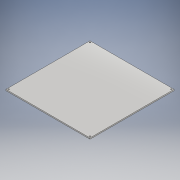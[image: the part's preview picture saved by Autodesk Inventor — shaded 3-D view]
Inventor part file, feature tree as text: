
AUTODESK INVENTOR PART (.ipt)
format: ipt  version: 2017 (Build 210142000, 142)  size: 108,032 bytes
history: native  units: mm
features: extrude x2, sketch x2, projected_geometry x1
ambient origin geometry x8: Origin, YZ Plane, XZ Plane, XY Plane, X Axis, Y Axis, Z Axis, Center Point
bodies: Solid1 (feature_tree)
feature tree (5):
  extrude  "Extrusion1"  Depth=3.0mm TaperAngle=0.0deg
  extrude  "Extrusion2"  Depth=3.0mm
  sketch  "Sketch1"  dims[d0=213.0mm d1=3.0mm d2=0.0mm]
  sketch  "Sketch2"  dims[d3=3.0mm d4=2.0mm d5=2.0mm d6=3.0mm d7=0.0mm]
  projected_geometry  "Projected Loop1"
